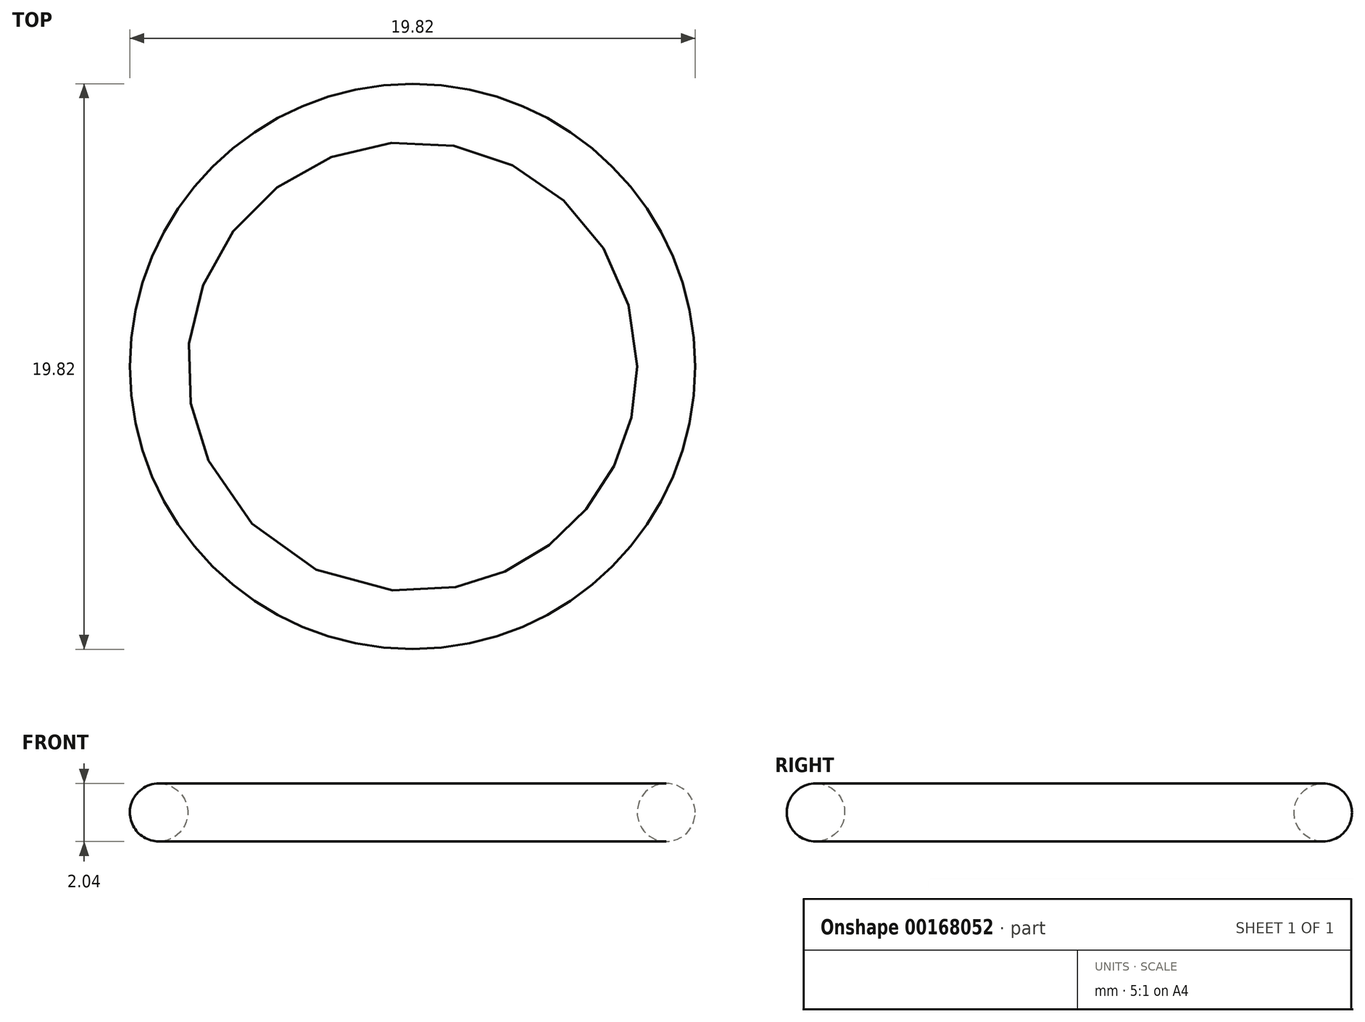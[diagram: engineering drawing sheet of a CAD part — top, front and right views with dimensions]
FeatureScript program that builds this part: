
annotation { "Feature Type Name" : "Feature", "Feature Type Description" : "" }
export const myFeature = defineFeature(function(context is Context, id is Id, definition is map)
    precondition{}
    {
        {
            var Q0;
            Q0=qCreatedBy(makeId("Front.planeOp"),FACE);
            var sketch = newSketch(context, id + "F0", { "sketchPlane" : qUnion([Q0])});
            skCircle(sketch, "E0", {"center": v(8.9, 0) * mm, "radius": 1.02 * mm});
            skLineSegment(sketch, "E1", {"start": v(0, 0) * mm, "end": v(0, -4.49) * mm, "construction": true});
            skSolve(sketch);
        }
        {
            var Q0;
            Q0=makeQuery(id+"F0.imprint","IMPRINT",FACE,{"disambiguationData":[TD([[makeQuery(id+"F0.imprint","IMPRINT",EDGE,{"derivedFrom":sQuery(id+"F0.wireOp",EDGE,"E0")}),1.0]])]});
            var Q1;
            Q1=sQuery(id+"F0.wireOp",EDGE,"E0");
            var Q2;
            Q2=sQuery(id+"F0.wireOp",EDGE,"E1");
            revolve(context, id + "F1", {"entities" : qUnion([Q0]), "surfaceEntities" : qUnion([Q1]), "axis" : qUnion([Q2]), "revolveType" : RevolveType.FULL});
        }
    });
